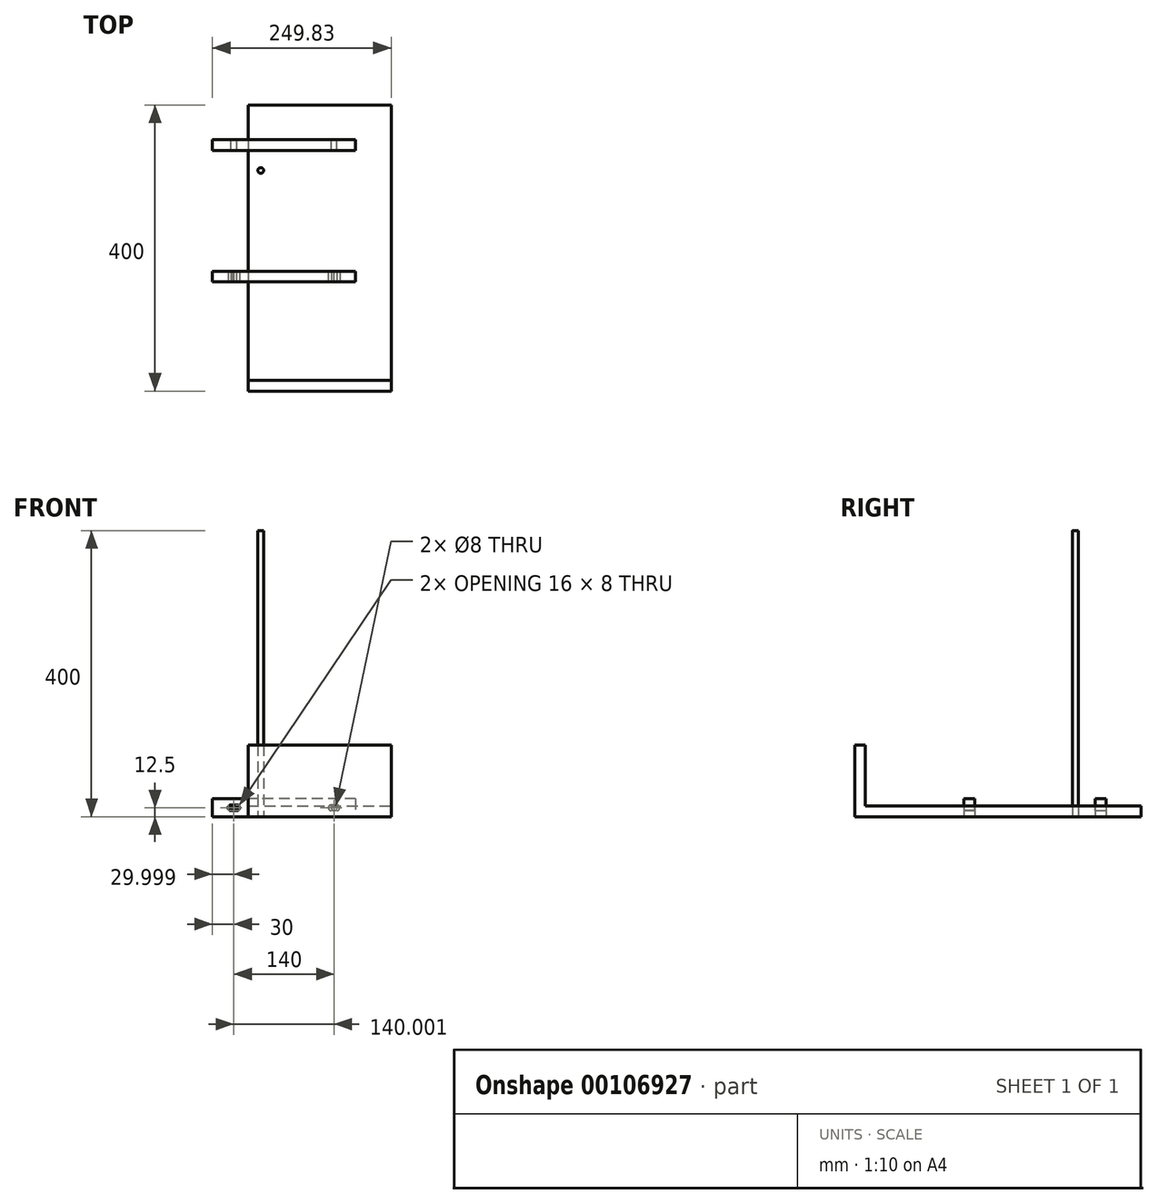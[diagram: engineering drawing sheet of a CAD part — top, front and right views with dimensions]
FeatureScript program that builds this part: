
annotation { "Feature Type Name" : "Feature", "Feature Type Description" : "" }
export const myFeature = defineFeature(function(context is Context, id is Id, definition is map)
    precondition{}
    {
        {
            var Q0;
            Q0=qCreatedBy(makeId("Top.planeOp"),FACE);
            var sketch = newSketch(context, id + "F0", { "sketchPlane" : qUnion([Q0])});
            skLineSegment(sketch, "E0.bottom", {"start": v(100, 84.6) * mm, "end": v(-100, 84.6) * mm});
            skLineSegment(sketch, "E0.top", {"start": v(100, 99.6) * mm, "end": v(-100, 99.6) * mm});
            skLineSegment(sketch, "E0.left", {"start": v(100, 84.6) * mm, "end": v(100, 99.6) * mm});
            skLineSegment(sketch, "E0.right", {"start": v(-100, 84.6) * mm, "end": v(-100, 99.6) * mm});
            skPoint(sketch, "E0.middle", {"position": v(0, 92.1) * mm});
            skLineSegment(sketch, "E1.bottom", {"start": v(100, -99.14) * mm, "end": v(-100, -99.14) * mm});
            skLineSegment(sketch, "E1.top", {"start": v(100, -84.14) * mm, "end": v(-100, -84.14) * mm});
            skLineSegment(sketch, "E1.left", {"start": v(100, -99.14) * mm, "end": v(100, -84.14) * mm});
            skLineSegment(sketch, "E1.right", {"start": v(-100, -99.14) * mm, "end": v(-100, -84.14) * mm});
            skPoint(sketch, "E1.middle", {"position": v(0, -91.64) * mm});
            skSolve(sketch);
        }
        {
            var Q0;
            Q0 = qSketchRegion(id + "F0", true);
            extrude(context, id + "F1", {"entities" : qUnion([Q0]), "depth" : 25 * mm});
        }
        {
            var Q0;
            Q0=makeQuery(id+"F1.opExtrude","SWEPT_FACE",FACE,{"disambiguationData":[OSD([sQuery(id+"F0.wireOp",EDGE,"E0.top")])]});
            var sketch = newSketch(context, id + "F2", { "sketchPlane" : qUnion([Q0])});
            skCircle(sketch, "E2", {"center": v(-70, 12.5) * mm, "radius": 4 * mm});
            skPoint(sketch, "E2.centerSnap0", {"position": v(-100, 12.5) * mm});
            skCircle(sketch, "E3", {"center": v(70, 12.5) * mm, "radius": 4 * mm});
            skPoint(sketch, "E3.centerSnap0", {"position": v(100, 12.5) * mm});
            skSolve(sketch);
        }
        {
            var Q0;
            Q0 = qSketchRegion(id + "F2", true);
            extrude(context, id + "F3", {"entities" : qUnion([Q0]), "operationType" : NewBodyOperationType.REMOVE, "oppositeDirection" : true, "depth" : 400 * mm});
        }
        {
            var Q0;
            Q0=qCreatedBy(makeId("Top.planeOp"),FACE);
            var sketch = newSketch(context, id + "F4", { "sketchPlane" : qUnion([Q0])});
            skCircle(sketch, "E4", {"center": v(-32.46, 56.74) * mm, "radius": 4 * mm});
            skSolve(sketch);
        }
        {
            var Q0;
            Q0 = qSketchRegion(id + "F4", true);
            extrude(context, id + "F5", {"entities" : qUnion([Q0]), "depth" : 400 * mm});
        }
        {
            var Q0;
            Q0=makeQuery(id+"F1.opExtrude","SWEPT_FACE",FACE,{"disambiguationData":[OSD([sQuery(id+"F0.wireOp",EDGE,"E1.bottom")])]});
            var sketch = newSketch(context, id + "F6", { "sketchPlane" : qUnion([Q0])});
            skLineSegment(sketch, "E5", {"start": v(-100, 12.5) * mm, "end": v(100, 12.5) * mm});
            skCircle(sketch, "E6", {"center": v(-74, 12.5) * mm, "radius": 4 * mm});
            skCircle(sketch, "E7", {"center": v(-66, 12.5) * mm, "radius": 4 * mm});
            skLineSegment(sketch, "E8", {"start": v(-73.74, 16.5) * mm, "end": v(-66.26, 16.5) * mm});
            skLineSegment(sketch, "E9", {"start": v(-73.92, 8.5) * mm, "end": v(-66, 8.5) * mm});
            skCircle(sketch, "E10.MirrorC", {"center": v(74, 12.5) * mm, "radius": 4 * mm});
            skLineSegment(sketch, "E11.MirrorCS", {"start": v(73.92, 8.5) * mm, "end": v(66, 8.5) * mm});
            skCircle(sketch, "E12.MirrorC", {"center": v(66, 12.5) * mm, "radius": 4 * mm});
            skLineSegment(sketch, "E13.MirrorCS", {"start": v(73.74, 16.5) * mm, "end": v(66.26, 16.5) * mm});
            skSolve(sketch);
        }
        {
            var Q0;
            Q0 = qSketchRegion(id + "F6", true);
            extrude(context, id + "F7", {"entities" : qUnion([Q0]), "operationType" : NewBodyOperationType.REMOVE, "oppositeDirection" : true, "depth" : 25 * mm});
        }
        {
            var Q0;
            Q0=qCreatedBy(makeId("Top.planeOp"),FACE);
            var sketch = newSketch(context, id + "F8", { "sketchPlane" : qUnion([Q0])});
            skLineSegment(sketch, "E14.bottom", {"start": v(-50.17, 148.3) * mm, "end": v(149.83, 148.3) * mm});
            skLineSegment(sketch, "E14.top", {"start": v(-50.17, -251.7) * mm, "end": v(149.83, -251.7) * mm});
            skLineSegment(sketch, "E14.left", {"start": v(-50.17, 148.3) * mm, "end": v(-50.17, -251.7) * mm});
            skLineSegment(sketch, "E14.right", {"start": v(149.83, 148.3) * mm, "end": v(149.83, -251.7) * mm});
            skSolve(sketch);
        }
        {
            var Q0;
            Q0 = qSketchRegion(id + "F8", true);
            extrude(context, id + "F9", {"entities" : qUnion([Q0]), "depth" : 15 * mm});
        }
        {
            var Q0;
            Q0=makeQuery(id+"F9.opExtrude","CAP_FACE",FACE,{"disambiguationData":[OSD([sQuery(id+"F8.wireOp",EDGE,"E14.bottom"),sQuery(id+"F8.wireOp",EDGE,"E14.top"),sQuery(id+"F8.wireOp",EDGE,"E14.left"),sQuery(id+"F8.wireOp",EDGE,"E14.right")])],"isStart":true});
            var sketch = newSketch(context, id + "F10", { "sketchPlane" : qUnion([Q0])});
            skPoint(sketch, "E15", {"position": v(-20.17, 221.7) * mm});
            skPoint(sketch, "E16", {"position": v(-20.17, 131.7) * mm});
            skLineSegment(sketch, "E17", {"start": v(49.83, 251.7) * mm, "end": v(49.83, 198.8) * mm});
            skPoint(sketch, "E18.MirrorP", {"position": v(119.83, 221.7) * mm});
            skPoint(sketch, "E19.MirrorP", {"position": v(119.83, 131.7) * mm});
            skSolve(sketch);
        }
        {
            var Q0;
            Q0=makeQuery(id+"F10.imprint","IMPRINT",FACE,{"disambiguationData":[TD([[makeQuery(id+"F10.imprint","IMPRINT",EDGE,{"derivedFrom":makeQuery(id+"F9.opExtrude","CAP_EDGE",EDGE,{"disambiguationData":[OSD([sQuery(id+"F8.wireOp",EDGE,"E14.bottom")])],"isStart":true})}),1.0]])]});
            var sketch = newSketch(context, id + "F11", { "sketchPlane" : qUnion([Q0])});
            skLineSegment(sketch, "E20.0.0", {"start": v(-50.17, 251.7) * mm, "end": v(-50.17, -148.3) * mm});
            skLineSegment(sketch, "E20.0.1", {"start": v(-50.17, -148.3) * mm, "end": v(149.83, -148.3) * mm});
            skLineSegment(sketch, "E20.0.2", {"start": v(149.83, -148.3) * mm, "end": v(149.83, 251.7) * mm});
            skLineSegment(sketch, "E20.0.3", {"start": v(149.83, 251.7) * mm, "end": v(49.83, 251.7) * mm});
            skLineSegment(sketch, "E20.0.4", {"start": v(49.83, 251.7) * mm, "end": v(-50.17, 251.7) * mm});
            skLineSegment(sketch, "E21", {"start": v(149.83, 236.7) * mm, "end": v(-50.17, 236.7) * mm});
            skSolve(sketch);
        }
        {
            var Q0;
            {var subQ1=sQuery(id+"F11.wireOp",EDGE,"E20.0.3");Q0=makeQuery(id+"F11.imprint","IMPRINT",FACE,{"disambiguationData":[TD([[makeQuery(id+"F11.imprint","IMPRINT",EDGE,{"derivedFrom":subQ1}),-1.0]])]});}
            extrude(context, id + "F12", {"entities" : qUnion([Q0]), "operationType" : NewBodyOperationType.ADD, "oppositeDirection" : true, "depth" : 100 * mm});
        }
    });
